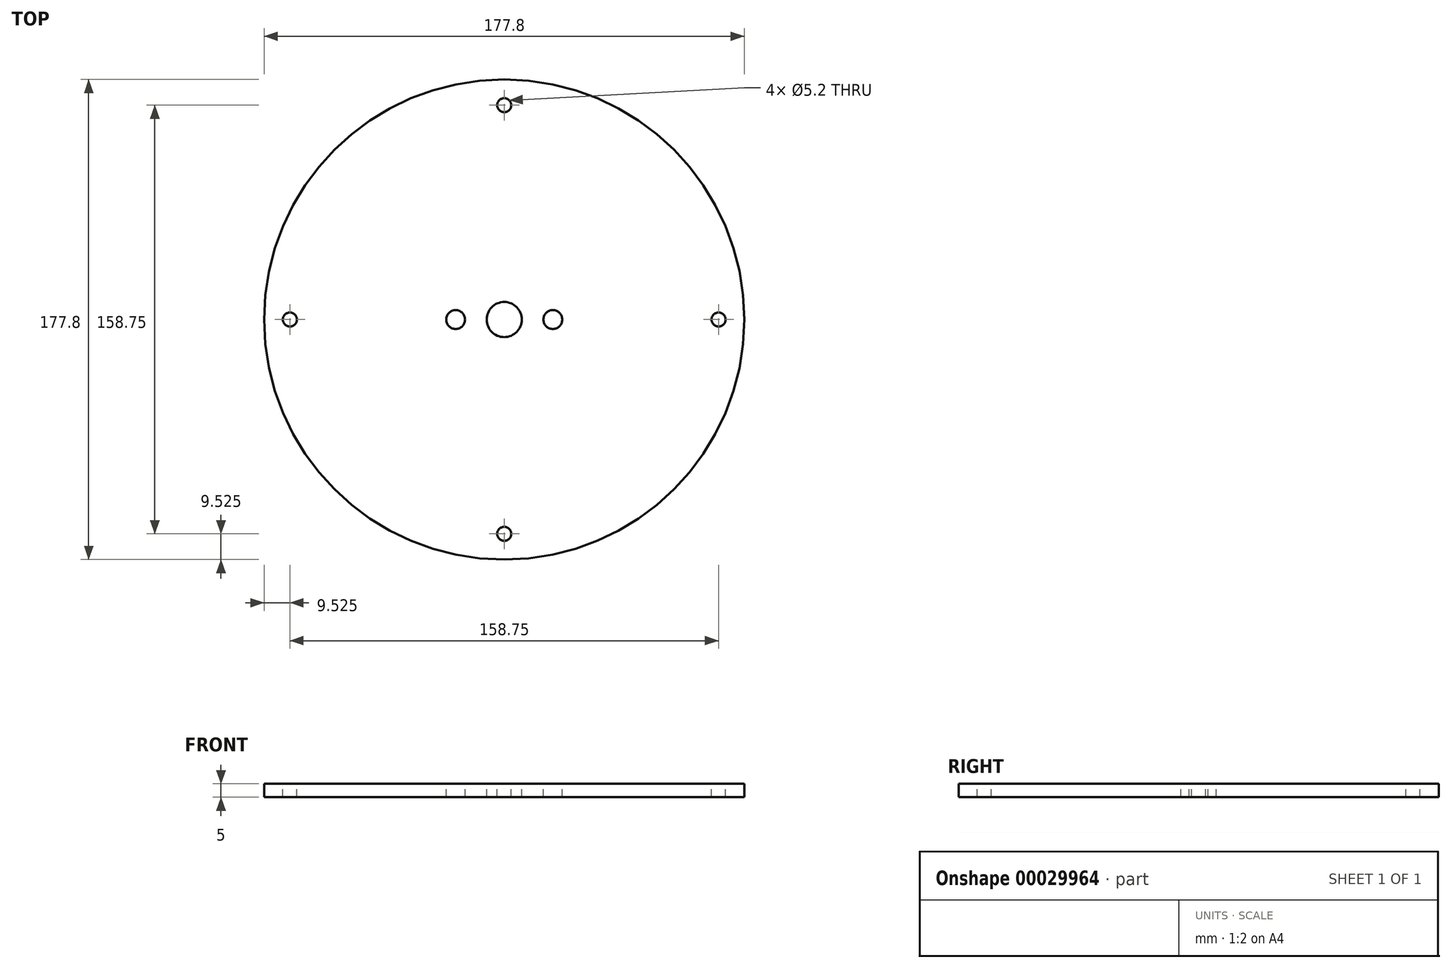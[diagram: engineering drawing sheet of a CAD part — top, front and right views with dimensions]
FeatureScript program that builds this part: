
annotation { "Feature Type Name" : "Feature", "Feature Type Description" : "" }
export const myFeature = defineFeature(function(context is Context, id is Id, definition is map)
    precondition{}
    {
        {
            var Q0;
            Q0=qCreatedBy(makeId("Top.planeOp"),FACE);
            var sketch = newSketch(context, id + "F0", { "sketchPlane" : qUnion([Q0])});
            skCircle(sketch, "E0", {"center": v(0, 0) * mm, "radius": 88.9 * mm});
            skSolve(sketch);
        }
        {
            var Q0;
            Q0 = qSketchRegion(id + "F0", true);
            extrude(context, id + "F1", {"entities" : qUnion([Q0]), "depth" : 5 * mm});
        }
        {
            var Q0;
            Q0=makeQuery(id+"F1.opExtrude","CAP_FACE",FACE,{"disambiguationData":[OSD([sQuery(id+"F0.wireOp",EDGE,"E0")])],"isStart":false});
            var sketch = newSketch(context, id + "F2", { "sketchPlane" : qUnion([Q0])});
            skCircle(sketch, "E1", {"center": v(0, 0) * mm, "radius": 6.5 * mm});
            skCircle(sketch, "E2", {"center": v(0, 79.38) * mm, "radius": 2.6 * mm});
            skCircle(sketch, "E3.1.0", {"center": v(-79.38, 0) * mm, "radius": 2.6 * mm});
            skCircle(sketch, "E3.2.0", {"center": v(0, -79.38) * mm, "radius": 2.6 * mm});
            skCircle(sketch, "E3.3.0", {"center": v(79.38, 0) * mm, "radius": 2.6 * mm});
            skSolve(sketch);
        }
        {
            var Q0;
            Q0 = qSketchRegion(id + "F2", true);
            extrude(context, id + "F3", {"entities" : qUnion([Q0]), "operationType" : NewBodyOperationType.REMOVE, "endBound" : BoundingType.THROUGH_ALL, "oppositeDirection" : true, "depth" : 25 * mm});
        }
        {
            var Q0;
            Q0=makeQuery(id+"F1.opExtrude","CAP_FACE",FACE,{"disambiguationData":[OSD([sQuery(id+"F0.wireOp",EDGE,"E0")])],"isStart":false});
            var sketch = newSketch(context, id + "F4", { "sketchPlane" : qUnion([Q0])});
            skCircle(sketch, "E4", {"center": v(18, 0) * mm, "radius": 3.5 * mm});
            skCircle(sketch, "E5", {"center": v(-18, 0) * mm, "radius": 3.5 * mm});
            skSolve(sketch);
        }
        {
            var Q0;
            Q0 = qSketchRegion(id + "F4", true);
            extrude(context, id + "F5", {"entities" : qUnion([Q0]), "operationType" : NewBodyOperationType.REMOVE, "endBound" : BoundingType.THROUGH_ALL, "oppositeDirection" : true, "depth" : 25 * mm});
        }
    });
